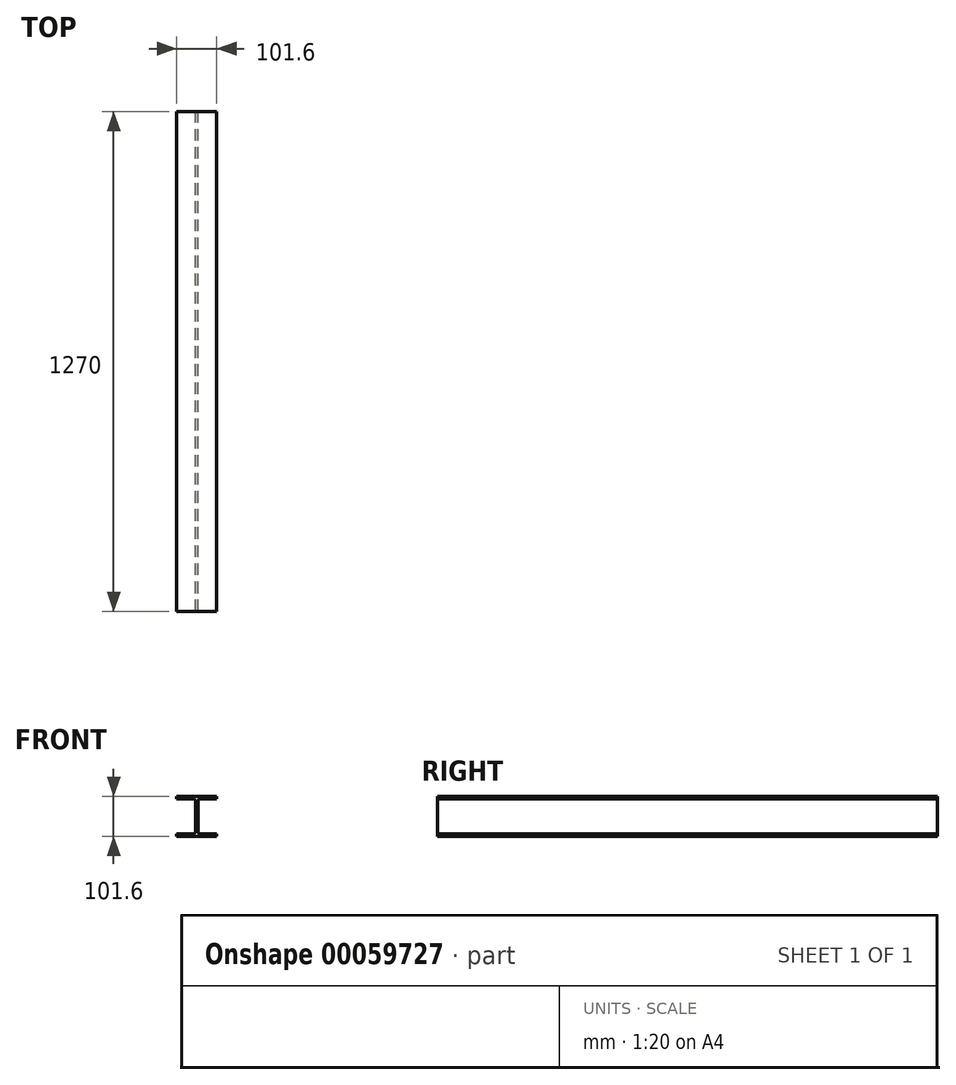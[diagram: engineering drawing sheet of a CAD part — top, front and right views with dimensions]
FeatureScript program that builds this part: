
annotation { "Feature Type Name" : "Feature", "Feature Type Description" : "" }
export const myFeature = defineFeature(function(context is Context, id is Id, definition is map)
    precondition{}
    {
        {
            var Q0;
            Q0=qCreatedBy(makeId("Front.planeOp"),FACE);
            var sketch = newSketch(context, id + "F0", { "sketchPlane" : qUnion([Q0])});
            skLineSegment(sketch, "E0", {"start": v(0, 48.72) * mm, "end": v(0, -49.32) * mm, "construction": true});
            skLineSegment(sketch, "E1", {"start": v(-51.25, 0) * mm, "end": v(44.4, 0) * mm, "construction": true});
            skLineSegment(sketch, "E2", {"start": v(0, 50.8) * mm, "end": v(50.8, 50.8) * mm});
            skLineSegment(sketch, "E3", {"start": v(50.8, 50.8) * mm, "end": v(50.8, 44.45) * mm});
            skLineSegment(sketch, "E4", {"start": v(50.8, 44.45) * mm, "end": v(9.52, 44.45) * mm});
            skLineSegment(sketch, "E5", {"start": v(3.18, 38.1) * mm, "end": v(3.18, 0) * mm});
            skPoint(sketch, "E6.visualSharp", {"position": v(3.18, 44.45) * mm});
            skArc(sketch, "E6.filletArc", {"start": v(9.52, 44.45) * mm, "mid": v(5.03, 42.6) * mm, "end": v(3.17, 38.1) * mm});
            skLineSegment(sketch, "E7.MirrorCS", {"start": v(-50.8, 50.8) * mm, "end": v(-50.8, 44.45) * mm});
            skArc(sketch, "E8.MirrorCS", {"start": v(-9.52, 44.45) * mm, "mid": v(-5.03, 42.6) * mm, "end": v(-3.17, 38.1) * mm});
            skLineSegment(sketch, "E9.MirrorCS", {"start": v(51.25, 0) * mm, "end": v(-44.4, 0) * mm, "construction": true});
            skLineSegment(sketch, "E10.MirrorCS", {"start": v(0, 50.8) * mm, "end": v(-50.8, 50.8) * mm});
            skPoint(sketch, "E11.MirrorP", {"position": v(-3.18, 44.45) * mm});
            skLineSegment(sketch, "E12.MirrorCS", {"start": v(-50.8, 44.45) * mm, "end": v(-9.52, 44.45) * mm});
            skLineSegment(sketch, "E13.MirrorCS", {"start": v(-3.18, 38.1) * mm, "end": v(-3.18, 0) * mm});
            skLineSegment(sketch, "E14.MirrorCS", {"start": v(50.8, -50.8) * mm, "end": v(50.8, -44.45) * mm});
            skLineSegment(sketch, "E15.MirrorCS", {"start": v(-50.8, -50.8) * mm, "end": v(-50.8, -44.45) * mm});
            skArc(sketch, "E16.MirrorCS", {"start": v(-9.53, -44.45) * mm, "mid": v(-5.03, -42.6) * mm, "end": v(-3.17, -38.1) * mm});
            skArc(sketch, "E17.MirrorCS", {"start": v(9.52, -44.45) * mm, "mid": v(5.03, -42.6) * mm, "end": v(3.17, -38.1) * mm});
            skLineSegment(sketch, "E18.MirrorCS", {"start": v(-3.18, -38.1) * mm, "end": v(-3.18, 0) * mm});
            skLineSegment(sketch, "E19.MirrorCS", {"start": v(0, -50.8) * mm, "end": v(-50.8, -50.8) * mm});
            skLineSegment(sketch, "E20.MirrorCS", {"start": v(3.17, -38.1) * mm, "end": v(3.18, 0) * mm});
            skPoint(sketch, "E21.MirrorP", {"position": v(3.17, -44.45) * mm});
            skLineSegment(sketch, "E22.MirrorCS", {"start": v(-50.8, -44.45) * mm, "end": v(-9.53, -44.45) * mm});
            skLineSegment(sketch, "E23.MirrorCS", {"start": v(0, -50.8) * mm, "end": v(50.8, -50.8) * mm});
            skLineSegment(sketch, "E24.MirrorCS", {"start": v(50.8, -44.45) * mm, "end": v(9.52, -44.45) * mm});
            skPoint(sketch, "E25.MirrorP", {"position": v(-3.18, -44.45) * mm});
            skSolve(sketch);
        }
        {
            var Q0;
            Q0=makeQuery(id+"F0.imprint","IMPRINT",FACE,{"disambiguationData":[TD([[makeQuery(id+"F0.imprint","IMPRINT",EDGE,{"derivedFrom":sQuery(id+"F0.wireOp",EDGE,"E7.MirrorCS")}),1.0]])]});
            extrude(context, id + "F1", {"entities" : qUnion([Q0]), "depth" : 1270 * mm});
        }
    });
